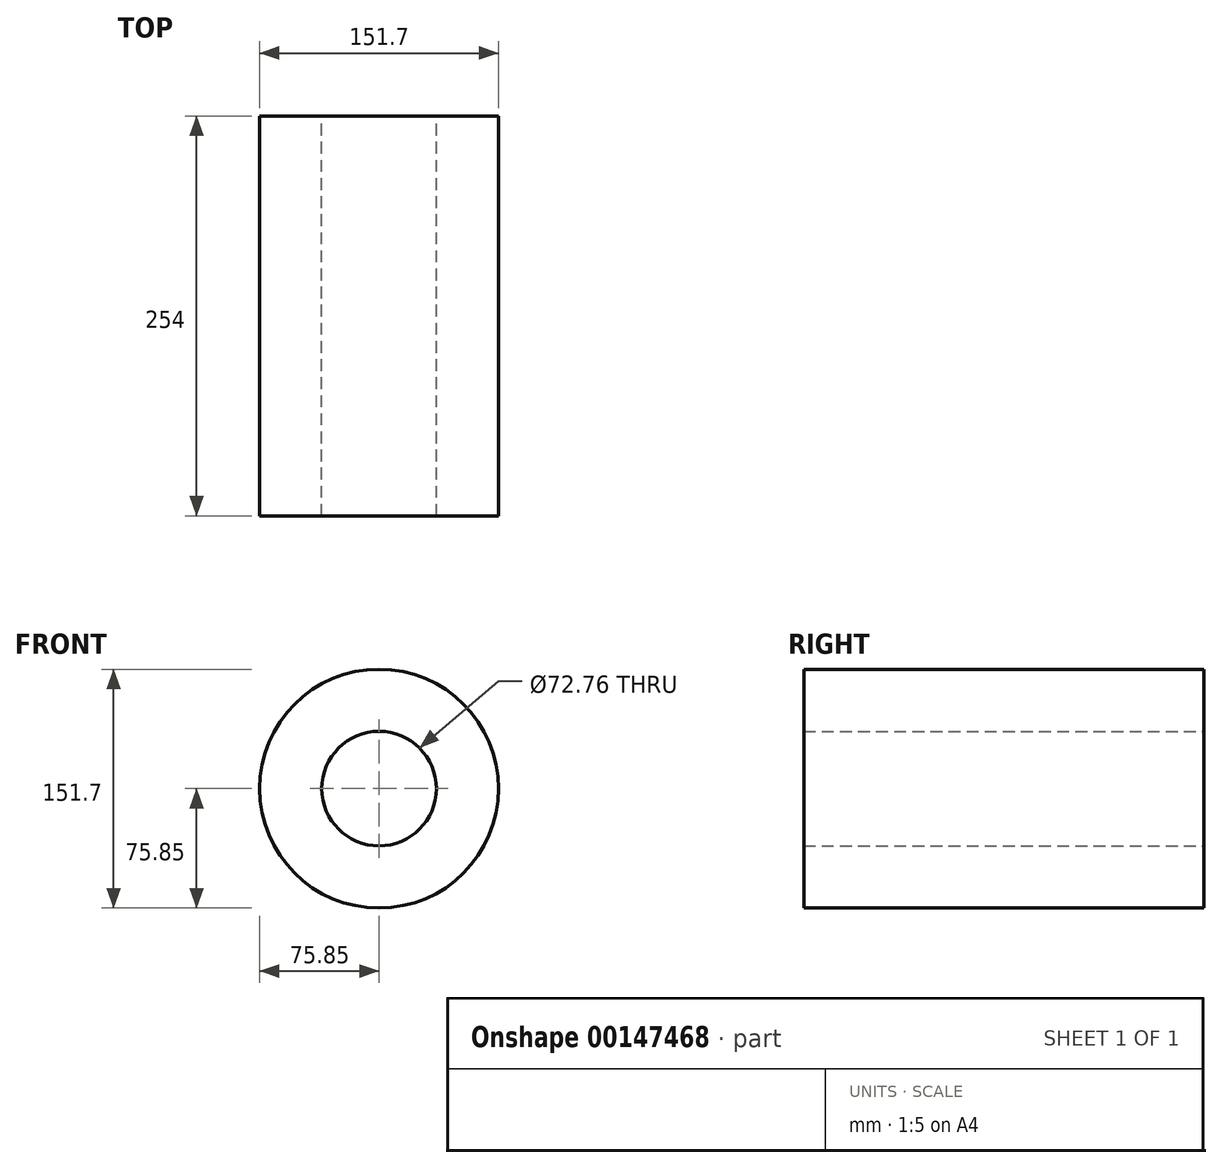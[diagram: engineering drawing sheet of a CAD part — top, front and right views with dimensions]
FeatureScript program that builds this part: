
annotation { "Feature Type Name" : "Feature", "Feature Type Description" : "" }
export const myFeature = defineFeature(function(context is Context, id is Id, definition is map)
    precondition{}
    {
        {
            var Q0;
            Q0=qCreatedBy(makeId("Front.planeOp"),FACE);
            var sketch = newSketch(context, id + "F0", { "sketchPlane" : qUnion([Q0])});
            skCircle(sketch, "E0", {"center": v(0, 0) * mm, "radius": 75.85 * mm});
            skCircle(sketch, "E1", {"center": v(0, 0) * mm, "radius": 36.38 * mm});
            skSolve(sketch);
        }
        {
            var Q0;
            Q0=makeQuery(id+"F0.imprint","IMPRINT",FACE,{"disambiguationData":[TD([[makeQuery(id+"F0.imprint","IMPRINT",EDGE,{"derivedFrom":sQuery(id+"F0.wireOp",EDGE,"E0")}),1.0]])]});
            extrude(context, id + "F1", {"entities" : qUnion([Q0]), "endBound" : BoundingType.SYMMETRIC, "depth" : 254 * mm});
        }
    });
